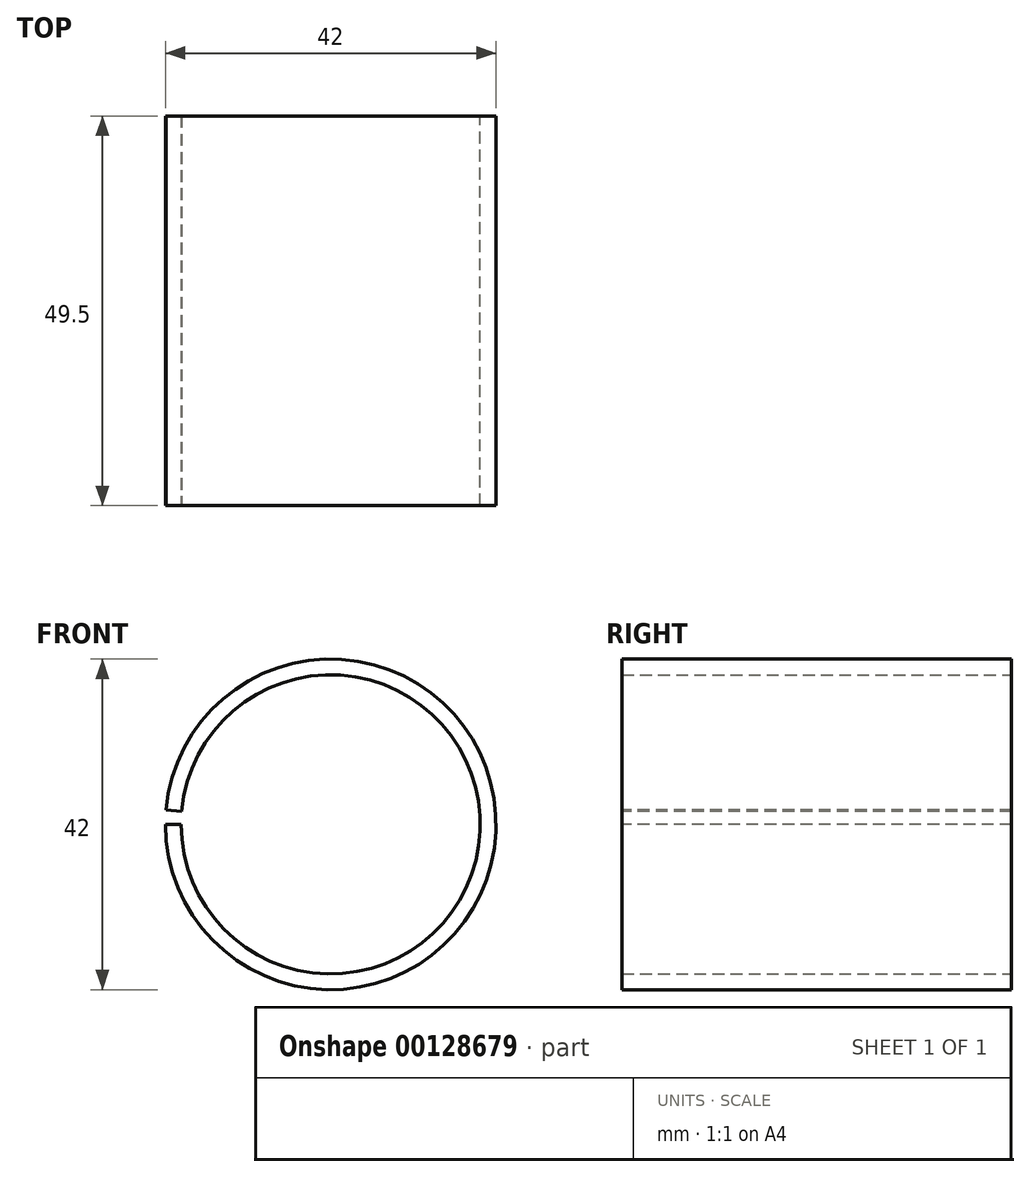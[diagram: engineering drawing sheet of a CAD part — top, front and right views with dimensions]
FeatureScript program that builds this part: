
annotation { "Feature Type Name" : "Feature", "Feature Type Description" : "" }
export const myFeature = defineFeature(function(context is Context, id is Id, definition is map)
    precondition{}
    {
        {
            var Q0;
            Q0=qCreatedBy(makeId("Top.planeOp"),FACE);
            var sketch = newSketch(context, id + "F0", { "sketchPlane" : qUnion([Q0])});
            skLineSegment(sketch, "E0", {"start": v(0, 0) * mm, "end": v(0, -80.08) * mm, "construction": true});
            skLineSegment(sketch, "E1.bottom", {"start": v(-21, 0) * mm, "end": v(-19, 0) * mm});
            skLineSegment(sketch, "E1.top", {"start": v(-21, -49.5) * mm, "end": v(-19, -49.5) * mm});
            skLineSegment(sketch, "E1.left", {"start": v(-21, 0) * mm, "end": v(-21, -49.5) * mm});
            skLineSegment(sketch, "E1.right", {"start": v(-19, 0) * mm, "end": v(-19, -49.5) * mm});
            skSolve(sketch);
        }
        {
            var Q0;
            Q0=makeQuery(id+"F0.imprint","IMPRINT",FACE,{"disambiguationData":[TD([[makeQuery(id+"F0.imprint","IMPRINT",EDGE,{"derivedFrom":sQuery(id+"F0.wireOp",EDGE,"E1.bottom")}),-1.0]])]});
            var Q1;
            Q1=sQuery(id+"F0.wireOp",EDGE,"E0");
            revolve(context, id + "F1", {"entities" : qUnion([Q0]), "axis" : qUnion([Q1]), "revolveType" : RevolveType.ONE_DIRECTION, "angle" : 355 * degree});
        }
    });
